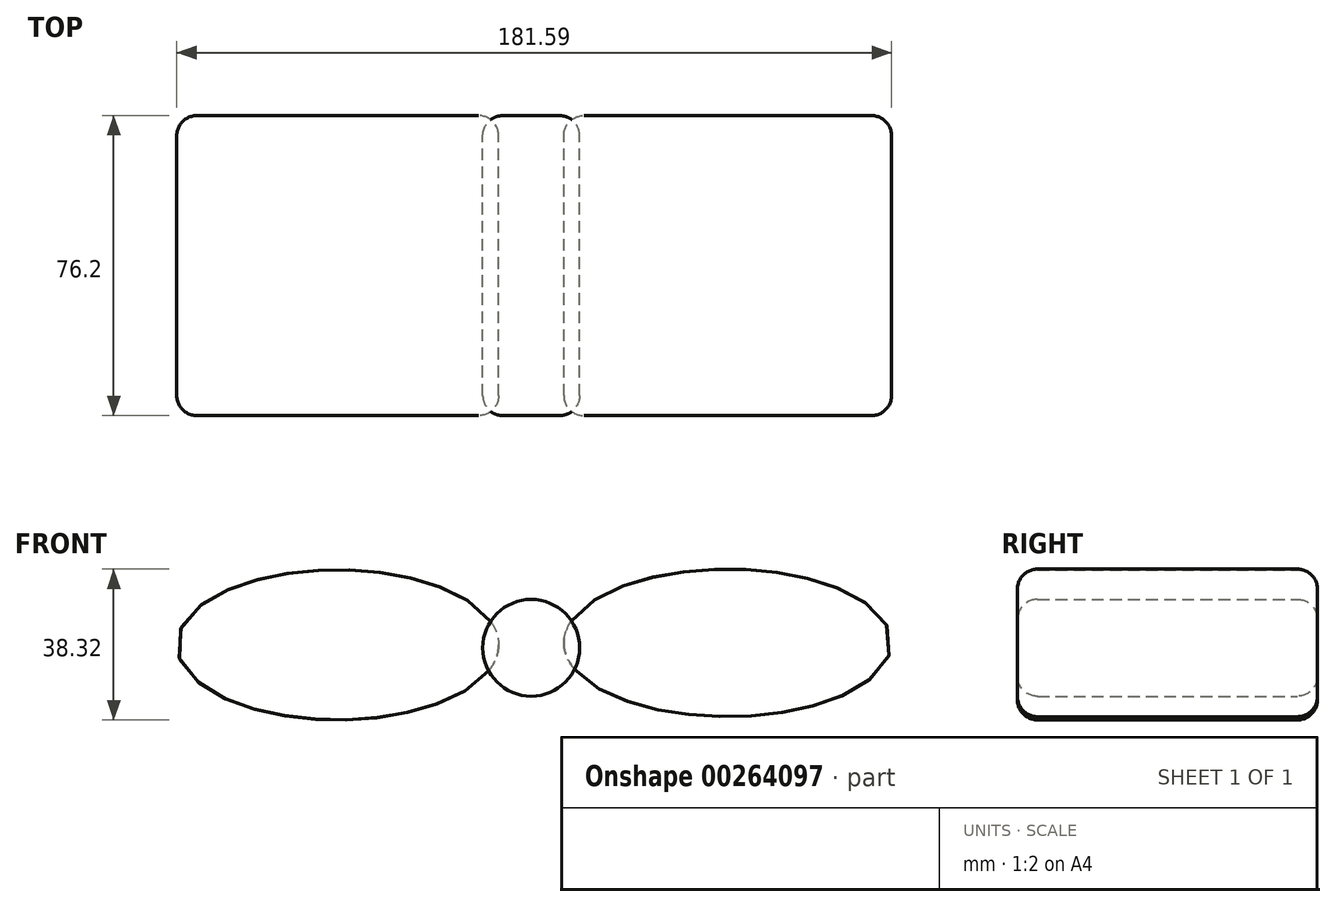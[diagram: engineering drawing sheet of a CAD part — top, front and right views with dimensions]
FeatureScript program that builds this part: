
annotation { "Feature Type Name" : "Feature", "Feature Type Description" : "" }
export const myFeature = defineFeature(function(context is Context, id is Id, definition is map)
    precondition{}
    {
        {
            var Q0;
            Q0=qCreatedBy(makeId("Front.planeOp"),FACE);
            var sketch = newSketch(context, id + "F0", { "sketchPlane" : qUnion([Q0])});
            skEllipse(sketch, "E0", {"center": v(-63.2, 9.53) * mm, "majorRadius": 40.88 * mm, "minorRadius": 19.06 * mm, "majorAxis": v(1, 0)});
            skEllipse(sketch, "E1", {"center": v(35.87, 10.03) * mm, "majorRadius": 41.64 * mm, "minorRadius": 18.76 * mm, "majorAxis": v(-1, 0)});
            skSolve(sketch);
        }
        {
            var Q0;
            Q0=qCreatedBy(makeId("Front.planeOp"),FACE);
            var sketch = newSketch(context, id + "F1", { "sketchPlane" : qUnion([Q0])});
            skCircle(sketch, "E2", {"center": v(-14.05, 8.78) * mm, "radius": 12.3 * mm});
            skSolve(sketch);
        }
        {
            var Q0;
            Q0=makeQuery(id+"F0.imprint","IMPRINT",FACE,{"disambiguationData":[TD([[makeQuery(id+"F0.imprint","IMPRINT",EDGE,{"derivedFrom":sQuery(id+"F0.wireOp",EDGE,"E0")}),1.0]])]});
            var Q1;
            Q1=makeQuery(id+"F1.imprint","IMPRINT",FACE,{"disambiguationData":[TD([[makeQuery(id+"F1.imprint","IMPRINT",EDGE,{"derivedFrom":sQuery(id+"F1.wireOp",EDGE,"E2")}),1.0]])]});
            var Q2;
            Q2=makeQuery(id+"F0.imprint","IMPRINT",FACE,{"disambiguationData":[TD([[makeQuery(id+"F0.imprint","IMPRINT",EDGE,{"derivedFrom":sQuery(id+"F0.wireOp",EDGE,"E1")}),1.0]])]});
            extrude(context, id + "F2", {"entities" : qUnion([Q0, Q1, Q2]), "depth" : 76.2 * mm});
        }
        {
            var Q0;
            Q0=makeQuery(id+"F2.opExtrude","CAP_EDGE",EDGE,{"disambiguationData":[OSD([sQuery(id+"F1.wireOp",EDGE,"E2")])],"isStart":false});
            var Q1;
            Q1=makeQuery(id+"F2.opExtrude","CAP_EDGE",EDGE,{"disambiguationData":[OSD([sQuery(id+"F1.wireOp",EDGE,"E2")])],"isStart":true});
            fillet(context, id + "F3", {"entities" : qUnion([Q0, Q1]), "radius" : 5.08 * mm, "tangentPropagation" : true, "allowEdgeOverflow" : false});
        }
        {
            var Q0;
            Q0=makeQuery(id+"F2.opExtrude","CAP_EDGE",EDGE,{"disambiguationData":[OSD([sQuery(id+"F0.wireOp",EDGE,"E0")])],"isStart":true});
            var Q1;
            Q1=makeQuery(id+"F2.opExtrude","CAP_EDGE",EDGE,{"disambiguationData":[OSD([sQuery(id+"F0.wireOp",EDGE,"E1")])],"isStart":true});
            var Q2;
            Q2=makeQuery(id+"F2.opExtrude","CAP_EDGE",EDGE,{"disambiguationData":[OSD([sQuery(id+"F0.wireOp",EDGE,"E1")])],"isStart":false});
            var Q3;
            Q3=makeQuery(id+"F2.opExtrude","CAP_EDGE",EDGE,{"disambiguationData":[OSD([sQuery(id+"F0.wireOp",EDGE,"E0")])],"isStart":false});
            fillet(context, id + "F4", {"entities" : qUnion([Q0, Q1, Q2, Q3]), "radius" : 5.08 * mm, "tangentPropagation" : true, "allowEdgeOverflow" : false});
        }
    });
